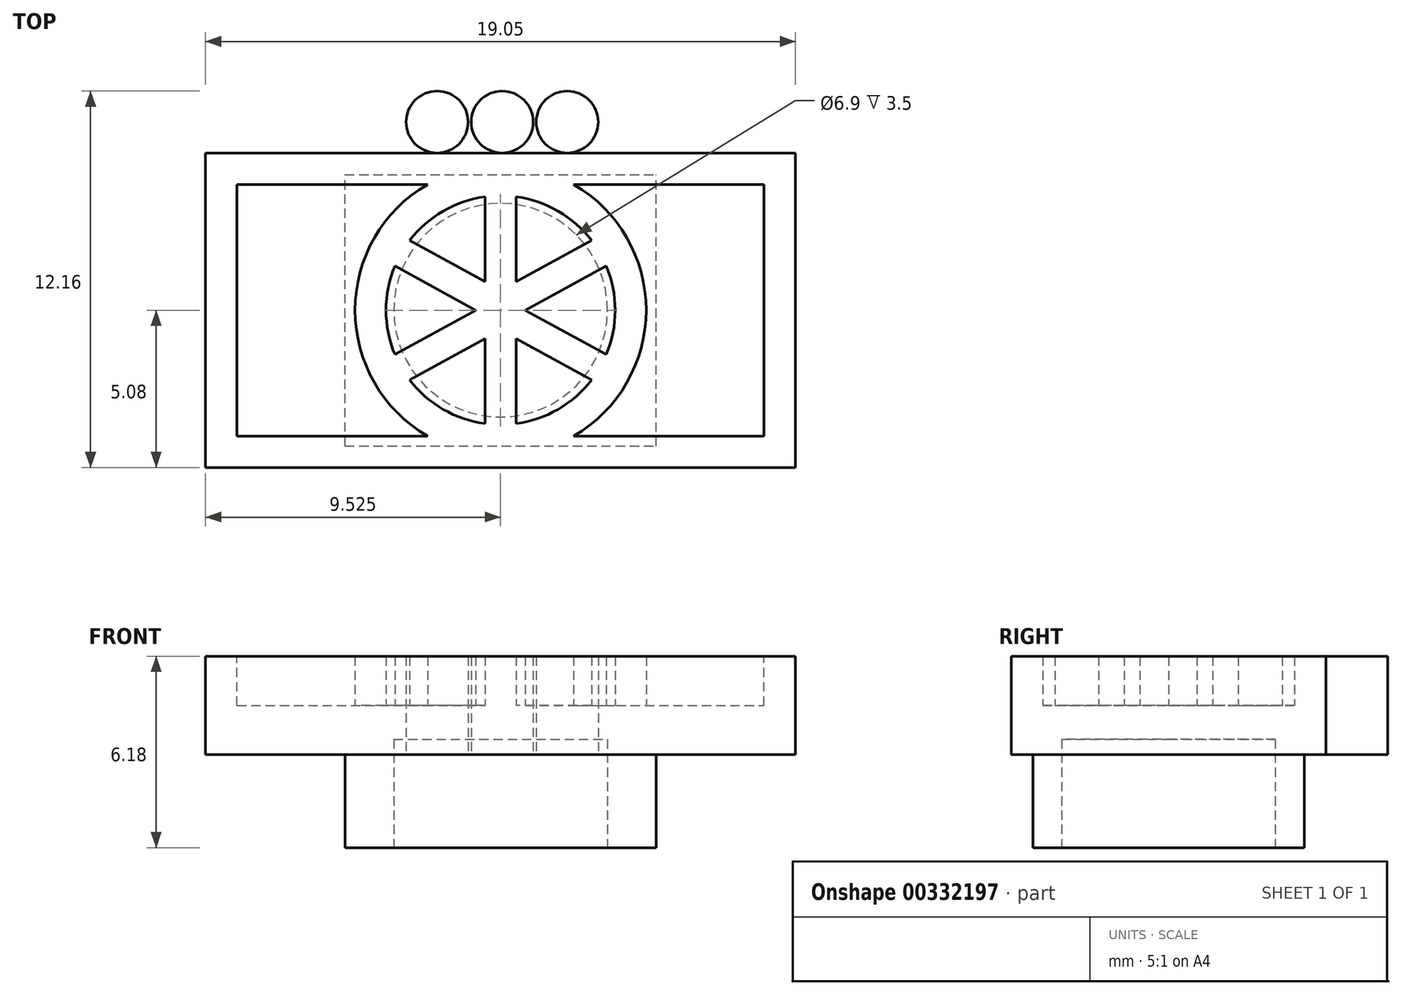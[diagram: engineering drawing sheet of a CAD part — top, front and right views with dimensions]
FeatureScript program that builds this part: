
annotation { "Feature Type Name" : "Feature", "Feature Type Description" : "" }
export const myFeature = defineFeature(function(context is Context, id is Id, definition is map)
    precondition{}
    {
        {
            var Q0;
            Q0=qCreatedBy(makeId("Top.planeOp"),FACE);
            var sketch = newSketch(context, id + "F0", { "sketchPlane" : qUnion([Q0])});
            skLineSegment(sketch, "E0.bottom", {"start": v(-19.05, 10.16) * mm, "end": v(0, 10.16) * mm});
            skLineSegment(sketch, "E0.top", {"start": v(-19.05, 0) * mm, "end": v(0, 0) * mm});
            skLineSegment(sketch, "E0.left", {"start": v(-19.05, 10.16) * mm, "end": v(-19.05, 0) * mm});
            skLineSegment(sketch, "E0.right", {"start": v(0, 10.16) * mm, "end": v(0, 0) * mm});
            skLineSegment(sketch, "E1", {"start": v(-9.52, 10.16) * mm, "end": v(-9.52, 0) * mm, "construction": true});
            skCircle(sketch, "E2", {"center": v(-9.48, 11.16) * mm, "radius": 1 * mm});
            skCircle(sketch, "E3", {"center": v(-11.58, 11.16) * mm, "radius": 1 * mm});
            skCircle(sketch, "E4.MirrorC", {"center": v(-7.38, 11.16) * mm, "radius": 1 * mm});
            skSolve(sketch);
        }
        {
            var Q0;
            Q0=qSketchRegion(id+"F0",true);
            extrude(context, id + "F1", {"entities" : qUnion([Q0]), "depth" : 3.17 * mm});
        }
        {
            var Q0;
            Q0=makeQuery(id+"F1.opExtrude","CAP_FACE",FACE,{"disambiguationData":[OSD([sQuery(id+"F0.wireOp",EDGE,"E0.bottom"),sQuery(id+"F0.wireOp",EDGE,"E0.top"),sQuery(id+"F0.wireOp",EDGE,"E0.left"),sQuery(id+"F0.wireOp",EDGE,"E0.right")])],"isStart":false});
            var sketch = newSketch(context, id + "F2", { "sketchPlane" : qUnion([Q0])});
            skLineSegment(sketch, "E5.bottom", {"start": v(-18.03, 9.14) * mm, "end": v(-1.02, 9.14) * mm});
            skLineSegment(sketch, "E5.top", {"start": v(-18.03, 1.02) * mm, "end": v(-1.02, 1.02) * mm});
            skLineSegment(sketch, "E5.left", {"start": v(-18.03, 9.14) * mm, "end": v(-18.03, 1.02) * mm});
            skLineSegment(sketch, "E5.right", {"start": v(-1.02, 9.14) * mm, "end": v(-1.02, 1.02) * mm});
            skSolve(sketch);
        }
        {
            var Q0;
            Q0=qSketchRegion(id+"F2",true);
            extrude(context, id + "F3", {"entities" : qUnion([Q0]), "operationType" : NewBodyOperationType.REMOVE, "oppositeDirection" : true, "depth" : 1.59 * mm});
        }
        {
            var Q0;
            {var subQ1=sQuery(id+"F2.wireOp",EDGE,"E5.top");var subQ4=makeQuery(id+"F3.boolean.opBoolean","COPY",FACE,{"derivedFrom":makeQuery(id+"F3.opExtrude","SWEPT_FACE",FACE,{"disambiguationData":[OSD([subQ1])]})});var subQ6=sQuery(id+"F2.wireOp",EDGE,"E5.right");Q0=makeQuery(id+"FbiU5rRMadnEj1Y_1.boolean.opBoolean","SPLIT",FACE,{"disambiguationData":[TD([subQ4])],"derivedFrom":makeQuery(id+"FD6hazfNaiJcgqe_1.boolean.opBoolean","SPLIT",FACE,{"disambiguationData":[TD([subQ4])],"derivedFrom":makeQuery(id+"F3.boolean.opBoolean","COPY",FACE,{"derivedFrom":makeQuery(id+"F3.opExtrude","CAP_FACE",FACE,{"disambiguationData":[OSD([sQuery(id+"F2.wireOp",EDGE,"E5.bottom"),subQ1,sQuery(id+"F2.wireOp",EDGE,"E5.left"),subQ6])],"isStart":false})})})});}
            var sketch = newSketch(context, id + "F4", { "sketchPlane" : qUnion([Q0])});
            skLineSegment(sketch, "E6", {"start": v(-19.05, 1.68) * mm, "end": v(-1.02, 1.68) * mm, "construction": true});
            skLineSegment(sketch, "E7", {"start": v(-9.53, 10.16) * mm, "end": v(-9.53, 0) * mm, "construction": true});
            skSolve(sketch);
        }
        {
            var Q0;
            Q0=makeQuery(id+"F1.opExtrude","CAP_FACE",FACE,{"disambiguationData":[OSD([sQuery(id+"F0.wireOp",EDGE,"E0.bottom"),sQuery(id+"F0.wireOp",EDGE,"E0.top"),sQuery(id+"F0.wireOp",EDGE,"E0.left"),sQuery(id+"F0.wireOp",EDGE,"E0.right"),sQuery(id+"F0.wireOp",EDGE,"iD4YVwzi-38ZZ-sZow-cuPB-LK5aPxXRs2tg"),sQuery(id+"F0.wireOp",EDGE,"25aa8db4-dd9b-41d2-b8c9-1594e9b75191"),sQuery(id+"F0.wireOp",EDGE,"40f63cb3-13d8-4821-a3c4-c05e674bd89b0.MirrorC")])],"isStart":true});
            var sketch = newSketch(context, id + "F5", { "sketchPlane" : qUnion([Q0])});
            skLineSegment(sketch, "E8.bottom", {"start": v(-14.55, -0.7) * mm, "end": v(-4.5, -0.7) * mm});
            skLineSegment(sketch, "E8.top", {"start": v(-14.55, -9.46) * mm, "end": v(-4.5, -9.46) * mm});
            skLineSegment(sketch, "E8.left", {"start": v(-14.55, -0.7) * mm, "end": v(-14.55, -9.46) * mm});
            skLineSegment(sketch, "E8.right", {"start": v(-4.5, -0.7) * mm, "end": v(-4.5, -9.46) * mm});
            skSolve(sketch);
        }
        {
            var Q0;
            Q0=qSketchRegion(id+"F5",true);
            extrude(context, id + "F6", {"entities" : qUnion([Q0]), "operationType" : NewBodyOperationType.ADD, "depth" : 3 * mm, "offsetDistance" : 25 * mm});
        }
        {
            var Q0;
            Q0=makeQuery(id+"F6.opExtrude","CAP_FACE",FACE,{"disambiguationData":[OSD([sQuery(id+"F5.wireOp",EDGE,"E8.bottom"),sQuery(id+"F5.wireOp",EDGE,"E8.top"),sQuery(id+"F5.wireOp",EDGE,"E8.left"),sQuery(id+"F5.wireOp",EDGE,"E8.right")])],"isStart":false});
            var sketch = newSketch(context, id + "F7", { "sketchPlane" : qUnion([Q0])});
            skCircle(sketch, "E9", {"center": v(-9.52, -5.08) * mm, "radius": 3.45 * mm});
            skLineSegment(sketch, "E10", {"start": v(-19.05, -5.08) * mm, "end": v(0, -5.08) * mm, "construction": true});
            skPoint(sketch, "E10.endSnap0", {"position": v(-4.5, -5.08) * mm});
            skLineSegment(sketch, "E11", {"start": v(-9.53, 0) * mm, "end": v(-9.53, -9.46) * mm, "construction": true});
            skSolve(sketch);
        }
        {
            var Q0;
            Q0=makeQuery(id+"F7.imprint","IMPRINT",FACE,{"disambiguationData":[TD([[makeQuery(id+"F7.imprint","IMPRINT",EDGE,{"derivedFrom":sQuery(id+"F7.wireOp",EDGE,"E9")}),1.0]])]});
            extrude(context, id + "F8", {"entities" : qUnion([Q0]), "operationType" : NewBodyOperationType.REMOVE, "oppositeDirection" : true, "depth" : 3.5 * mm, "offsetDistance" : 25 * mm});
        }
        {
            var Q0;
            Q0=makeQuery(id+"F4.imprint","IMPRINT",FACE,{"disambiguationData":[TD([[makeQuery(id+"F4.imprint","IMPRINT",EDGE,{"derivedFrom":makeQuery(id+"F3.boolean.opBoolean","COPY",EDGE,{"derivedFrom":makeQuery(id+"F3.opExtrude","CAP_EDGE",EDGE,{"disambiguationData":[OSD([sQuery(id+"F2.wireOp",EDGE,"E5.bottom")])],"isStart":false})})}),-1.0]])]});
            var sketch = newSketch(context, id + "F9", { "sketchPlane" : qUnion([Q0])});
            skLineSegment(sketch, "E12", {"start": v(-6.24, 7.53) * mm, "end": v(-9.53, 5.73) * mm});
            skLineSegment(sketch, "E13", {"start": v(-8.73, 5.08) * mm, "end": v(-5.54, 6.83) * mm});
            skLineSegment(sketch, "E14", {"start": v(-5.54, 6.83) * mm, "end": v(-5.54, 7.53) * mm});
            skLineSegment(sketch, "E15", {"start": v(-5.54, 7.53) * mm, "end": v(-6.24, 7.53) * mm});
            skLineSegment(sketch, "E16", {"start": v(-19.05, 5.08) * mm, "end": v(0, 5.08) * mm, "construction": true});
            skLineSegment(sketch, "E17.MirrorCS", {"start": v(-12.81, 7.53) * mm, "end": v(-9.53, 5.73) * mm});
            skLineSegment(sketch, "E18.MirrorCS", {"start": v(-10.33, 5.08) * mm, "end": v(-13.51, 6.83) * mm});
            skLineSegment(sketch, "E19.MirrorCS", {"start": v(-13.51, 6.83) * mm, "end": v(-13.51, 7.53) * mm});
            skLineSegment(sketch, "E20.MirrorCS", {"start": v(-13.51, 7.53) * mm, "end": v(-12.81, 7.53) * mm});
            skLineSegment(sketch, "E21.MirrorCS", {"start": v(-10.32, 5.08) * mm, "end": v(-13.51, 3.33) * mm});
            skLineSegment(sketch, "E22.MirrorCS", {"start": v(-8.72, 5.08) * mm, "end": v(-5.54, 3.33) * mm});
            skLineSegment(sketch, "E23.MirrorCS", {"start": v(-6.24, 2.63) * mm, "end": v(-9.53, 4.43) * mm});
            skLineSegment(sketch, "E24.MirrorCS", {"start": v(-12.81, 2.63) * mm, "end": v(-9.53, 4.43) * mm});
            skLineSegment(sketch, "E25.MirrorCS", {"start": v(-13.51, 2.63) * mm, "end": v(-12.81, 2.63) * mm});
            skLineSegment(sketch, "E26.MirrorCS", {"start": v(-13.51, 3.33) * mm, "end": v(-13.51, 2.63) * mm});
            skLineSegment(sketch, "E27.MirrorCS", {"start": v(-5.54, 3.33) * mm, "end": v(-5.54, 2.63) * mm});
            skLineSegment(sketch, "E28.MirrorCS", {"start": v(-5.54, 2.63) * mm, "end": v(-6.24, 2.63) * mm});
            skLineSegment(sketch, "E29.bottom", {"start": v(-10.03, 9.14) * mm, "end": v(-9.03, 9.14) * mm});
            skLineSegment(sketch, "E29.top", {"start": v(-10.03, 1.02) * mm, "end": v(-9.03, 1.02) * mm});
            skLineSegment(sketch, "E29.left", {"start": v(-10.03, 9.14) * mm, "end": v(-10.03, 1.02) * mm});
            skLineSegment(sketch, "E29.right", {"start": v(-9.03, 9.14) * mm, "end": v(-9.03, 1.02) * mm});
            skSolve(sketch);
        }
        {
            var Q0;
            Q0=qSketchRegion(id+"F9",true);
            var Q1;
            Q1=makeQuery(id+"FXsS83p9KQ4uv0L_1.boolean.opBoolean","MERGE",FACE,{"derivedFrom":[makeQuery(id+"F1.opExtrude","CAP_FACE",FACE,{"disambiguationData":[OSD([sQuery(id+"F0.wireOp",EDGE,"E0.bottom"),sQuery(id+"F0.wireOp",EDGE,"E0.top"),sQuery(id+"F0.wireOp",EDGE,"E0.left"),sQuery(id+"F0.wireOp",EDGE,"E0.right"),sQuery(id+"F0.wireOp",EDGE,"25aa8db4-dd9b-41d2-b8c9-1594e9b75191"),sQuery(id+"F0.wireOp",EDGE,"40f63cb3-13d8-4821-a3c4-c05e674bd89b0.MirrorC")])],"isStart":false}),makeQuery(id+"FbiU5rRMadnEj1Y_1.opExtrude","CAP_FACE",FACE,{"disambiguationData":[OSD([sQuery(id+"FmV1InaubWQgJeV_1.wireOp",EDGE,"lTleeF4S-0pnc-dI25-KJAR-2TLCTf0jWGc3"),sQuery(id+"FmV1InaubWQgJeV_1.wireOp",EDGE,"m9JDErra-axgF-Q1Zk-CJc0-x6RwavRCbCz8")])],"isStart":false}),makeQuery(id+"FXsS83p9KQ4uv0L_1.opExtrude","CAP_FACE",FACE,{"disambiguationData":[OSD([sQuery(id+"Fi3yzKCDt9pSW51_1.wireOp",EDGE,"cutzoVbR-JFbv-1kZ0-SQrw-pSLFGMZcN76v"),sQuery(id+"Fi3yzKCDt9pSW51_1.wireOp",EDGE,"XYQyWRLz-35l4-wHee-0FsY-Oat0KQk3jhR6"),sQuery(id+"Fi3yzKCDt9pSW51_1.wireOp",EDGE,"lBgadLLx-aQS8-kMAZ-d5qN-Zo8duSUxtBeX"),sQuery(id+"Fi3yzKCDt9pSW51_1.wireOp",EDGE,"DlRPRQGx-Alaq-SPUL-URFH-jddu6C2Nnp9z"),sQuery(id+"Fi3yzKCDt9pSW51_1.wireOp",EDGE,"Shc4e2eY-gIsf-lYKj-D0sO-212MCfLGw1w2"),sQuery(id+"Fi3yzKCDt9pSW51_1.wireOp",EDGE,"DXv1RSob-CDWK-uPmN-nh2c-bdjhB3yjVnB2"),sQuery(id+"Fi3yzKCDt9pSW51_1.wireOp",EDGE,"Mjf90MPI-7UZW-OfA1-fD3l-TGEU1IJ1uaYu"),sQuery(id+"Fi3yzKCDt9pSW51_1.wireOp",EDGE,"IrneLFi4-a4Xm-RgwH-oJvY-WcCPALNDAReP"),sQuery(id+"Fi3yzKCDt9pSW51_1.wireOp",EDGE,"toQdHavX-h7D1-dxbV-IXrh-P84p4AImceJh"),sQuery(id+"Fi3yzKCDt9pSW51_1.wireOp",EDGE,"xGw8HYbu-oKFY-4S3u-lNNy-w4TfAhwJFqQu"),sQuery(id+"Fi3yzKCDt9pSW51_1.wireOp",EDGE,"5pvZd2gl-M8UA-9HNZ-daD7-4TEjzgTyMgsA"),sQuery(id+"Fi3yzKCDt9pSW51_1.wireOp",EDGE,"b1702624-0c59-4015-bc2e-a5f6b81265a70.MirrorCS"),sQuery(id+"Fi3yzKCDt9pSW51_1.wireOp",EDGE,"7deeccc9-7886-4666-b44c-47b900ed28990.MirrorCS"),sQuery(id+"Fi3yzKCDt9pSW51_1.wireOp",EDGE,"75936777-967d-44d6-aacf-753113c8b50b0.MirrorCS"),sQuery(id+"Fi3yzKCDt9pSW51_1.wireOp",EDGE,"e5875930-5b2f-47d0-b261-f87a419dd3ea0.MirrorCS"),sQuery(id+"Fi3yzKCDt9pSW51_1.wireOp",EDGE,"e1f8200d-9078-41b5-85b4-8a4adb8dc9e80.MirrorCS"),sQuery(id+"Fi3yzKCDt9pSW51_1.wireOp",EDGE,"40fd4d9e-f758-4b42-b7b5-3e08d0cf58f50.MirrorCS"),sQuery(id+"Fi3yzKCDt9pSW51_1.wireOp",EDGE,"553d3a6c-e9a7-4b40-b1d3-0817f640e5cc0.MirrorCS"),sQuery(id+"Fi3yzKCDt9pSW51_1.wireOp",EDGE,"5a723a2c-c48e-43ea-a32e-a11b15ff1a7b0.MirrorCS"),sQuery(id+"Fi3yzKCDt9pSW51_1.wireOp",EDGE,"932d58c0-4b54-410d-a467-0e9cf49887c90.MirrorCS"),sQuery(id+"Fi3yzKCDt9pSW51_1.wireOp",EDGE,"eeedfdb4-aa26-4e83-bf33-b18388155c4d0.MirrorCS"),sQuery(id+"Fi3yzKCDt9pSW51_1.wireOp",EDGE,"a4c71cba-da55-4cc9-80cf-8947727491d80.MirrorCS")])],"isStart":false})]});
            extrude(context, id + "F10", {"entities" : qUnion([Q0]), "operationType" : NewBodyOperationType.ADD, "endBound" : BoundingType.UP_TO_SURFACE, "depth" : 25 * mm, "endBoundEntityFace" : qUnion([Q1]), "offsetDistance" : 25 * mm});
        }
        {
            var Q0;
            Q0=makeQuery(id+"F4.imprint","IMPRINT",FACE,{"disambiguationData":[TD([[makeQuery(id+"F4.imprint","IMPRINT",EDGE,{"derivedFrom":makeQuery(id+"F3.boolean.opBoolean","COPY",EDGE,{"derivedFrom":makeQuery(id+"F3.opExtrude","CAP_EDGE",EDGE,{"disambiguationData":[OSD([sQuery(id+"F2.wireOp",EDGE,"E5.bottom")])],"isStart":false})})}),-1.0]])]});
            var sketch = newSketch(context, id + "F11", { "sketchPlane" : qUnion([Q0])});
            skCircle(sketch, "E30", {"center": v(-9.53, 5.08) * mm, "radius": 3.7 * mm});
            skCircle(sketch, "E31", {"center": v(-9.53, 5.08) * mm, "radius": 4.7 * mm});
            skSolve(sketch);
        }
        {
            var Q0;
            Q0 = qSketchRegion(id + "F11", true);
            var Q1;
            Q1=makeQuery(id+"F10.boolean.opBoolean","MERGE",FACE,{"derivedFrom":[makeQuery(id+"F1.opExtrude","CAP_FACE",FACE,{"disambiguationData":[OSD([sQuery(id+"F0.wireOp",EDGE,"E0.bottom"),sQuery(id+"F0.wireOp",EDGE,"E0.top"),sQuery(id+"F0.wireOp",EDGE,"E0.left"),sQuery(id+"F0.wireOp",EDGE,"E0.right")])],"isStart":false}),makeQuery(id+"F10.opExtrude","CAP_FACE",FACE,{"disambiguationData":[OSD([sQuery(id+"F9.wireOp",EDGE,"E12"),sQuery(id+"F9.wireOp",EDGE,"E13"),sQuery(id+"F9.wireOp",EDGE,"E14"),sQuery(id+"F9.wireOp",EDGE,"E15"),sQuery(id+"F9.wireOp",EDGE,"E17.MirrorCS"),sQuery(id+"F9.wireOp",EDGE,"E18.MirrorCS"),sQuery(id+"F9.wireOp",EDGE,"E19.MirrorCS"),sQuery(id+"F9.wireOp",EDGE,"E20.MirrorCS"),sQuery(id+"F9.wireOp",EDGE,"E21.MirrorCS"),sQuery(id+"F9.wireOp",EDGE,"E22.MirrorCS"),sQuery(id+"F9.wireOp",EDGE,"E23.MirrorCS"),sQuery(id+"F9.wireOp",EDGE,"E24.MirrorCS"),sQuery(id+"F9.wireOp",EDGE,"E25.MirrorCS"),sQuery(id+"F9.wireOp",EDGE,"E26.MirrorCS"),sQuery(id+"F9.wireOp",EDGE,"E27.MirrorCS"),sQuery(id+"F9.wireOp",EDGE,"E28.MirrorCS"),sQuery(id+"F9.wireOp",EDGE,"E29.bottom"),sQuery(id+"F9.wireOp",EDGE,"E29.top"),sQuery(id+"F9.wireOp",EDGE,"E29.left"),sQuery(id+"F9.wireOp",EDGE,"E29.right")])],"isStart":false})]});
            extrude(context, id + "F12", {"entities" : qUnion([Q0]), "operationType" : NewBodyOperationType.ADD, "endBound" : BoundingType.UP_TO_SURFACE, "depth" : 25 * mm, "endBoundEntityFace" : qUnion([Q1]), "offsetDistance" : 25 * mm});
        }
    });
